# Revit family: Window-Double_Hung-Pella-Architect_Series-Vent
name_source: partatom
category: Windows
revit_build: Autodesk Revit Architecture 2013 (Build: 20130531_2115(x64)
units: mm (PartAtom-declared; Revit-internal decimal feet)

## types (80) — shared parameters
Analytic Construction = <None>
Architectural Design Manual = To be Determined
Construction Type = -
Cross Grille Pattern = No
Custom Grille Pattern = No
Custom Horizontal Lites = 2
Custom Vertical Lites = 3
Default Sill Height = 2' - 7 1/2"
Description = Double Hung - Vent Units
Egress Window = No
Energy Efficiency = http://www.pella.com
Environmental Commitment = http://www.pella.com
Ext Finish = Aluminum - Pella - Brown
Glazing Finish = Glass - Pella - Clear Insulating Glass
Glazing Thickness = 0' - 0 163/256"
Heat Transfer Coefficient (U) = 0.1000 BTU/(h·ft²·°F)
Int Finish = Wood - Pella - Pine
Lower Grille Visibility = Yes
Manufacturer = Pella Windows & Doors
Operation = Vent
Prairie Grille Pattern = No
Product Documentation Link = http://media.pella.com
Product Name = Architect Series Double-Hung Window
Product Page URL = http://www.pella.com
Series = Architect Series - Aluminum-Clad Wood
Size Constraint = Window Sizing constraints available in 6.35 mm increments
Thermal Resistance (R) = 10.0000 (h·ft²·°F)/BTU
Top Row Grille Pattern = No
Traditional Grille Pattern = Yes
URL = www.pella.com
Upper Grille Visibility = Yes
Wall Closure = By host
zero-valued in all types: Solar Heat Gain Coefficient, Visual Light Transmittance

## per-type parameters (varying)
| type | Bottom Pane Height | Checkrail Height | Head Height | Height | Rough Height | Rough Width | Unit Height | Unit Width | Width |
| 2135 | 1' - 5 15/64" | 1' - 5 7/8" | 5' - 6 1/2" | 2' - 11" | 2' - 11 3/4" | 1' - 9 3/4" | 2' - 11" | 1' - 9" | 1' - 9" |
| 2141 | 1' - 8 15/64" | 1' - 8 7/8" | 6' - 0 1/2" | 3' - 5" | 3' - 5 3/4" | 1' - 9 3/4" | 3' - 5" | 1' - 9" | 1' - 9" |
| 2147 | 1' - 11 15/64" | 1' - 11 7/8" | 6' - 6 1/2" | 3' - 11" | 3' - 11 3/4" | 1' - 9 3/4" | 3' - 11" | 1' - 9" | 1' - 9" |
| 2153 | 2' - 2 15/64" | 2' - 2 7/8" | 7' - 0 1/2" | 4' - 5" | 4' - 5 3/4" | 1' - 9 3/4" | 4' - 5" | 1' - 9" | 1' - 9" |
| 2157 | 2' - 4 15/64" | 2' - 4 7/8" | 7' - 4 1/2" | 4' - 9" | 4' - 9 3/4" | 1' - 9 3/4" | 4' - 9" | 1' - 9" | 1' - 9" |
| 2159 | 2' - 5 15/64" | 2' - 5 7/8" | 7' - 6 1/2" | 4' - 11" | 4' - 11 3/4" | 1' - 9 3/4" | 4' - 11" | 1' - 9" | 1' - 9" |
| 2165 | 2' - 8 15/64" | 2' - 8 7/8" | 8' - 0 1/2" | 5' - 5" | 5' - 5 3/4" | 1' - 9 3/4" | 5' - 5" | 1' - 9" | 1' - 9" |
| 2171 | 2' - 11 15/64" | 2' - 11 7/8" | 8' - 6 1/2" | 5' - 11" | 5' - 11 3/4" | 1' - 9 3/4" | 5' - 11" | 1' - 9" | 1' - 9" |
| 2177 | 3' - 2 15/64" | 3' - 2 7/8" | 9' - 0 1/2" | 6' - 5" | 6' - 5 3/4" | 1' - 9 3/4" | 6' - 5" | 1' - 9" | 1' - 9" |
| 2184 | 3' - 5 47/64" | 3' - 6 3/8" | 9' - 7 1/2" | 7' - 0" | 7' - 0 3/4" | 1' - 9 3/4" | 7' - 0" | 1' - 9" | 1' - 9" |
| 2535 | 1' - 5 15/64" | 1' - 5 7/8" | 5' - 6 1/2" | 2' - 11" | 2' - 11 3/4" | 2' - 1 3/4" | 2' - 11" | 2' - 1" | 2' - 1" |
| 2541 | 1' - 8 15/64" | 1' - 8 7/8" | 6' - 0 1/2" | 3' - 5" | 3' - 5 3/4" | 2' - 1 3/4" | 3' - 5" | 2' - 1" | 2' - 1" |
| 2547 | 1' - 11 15/64" | 1' - 11 7/8" | 6' - 6 1/2" | 3' - 11" | 3' - 11 3/4" | 2' - 1 3/4" | 3' - 11" | 2' - 1" | 2' - 1" |
| 2553 | 2' - 2 15/64" | 2' - 2 7/8" | 7' - 0 1/2" | 4' - 5" | 4' - 5 3/4" | 2' - 1 3/4" | 4' - 5" | 2' - 1" | 2' - 1" |
| 2557 | 2' - 4 15/64" | 2' - 4 7/8" | 7' - 4 1/2" | 4' - 9" | 4' - 9 3/4" | 2' - 1 3/4" | 4' - 9" | 2' - 1" | 2' - 1" |
| 2559 | 2' - 5 15/64" | 2' - 5 7/8" | 7' - 6 1/2" | 4' - 11" | 4' - 11 3/4" | 2' - 1 3/4" | 4' - 11" | 2' - 1" | 2' - 1" |
| 2565 | 2' - 8 15/64" | 2' - 8 7/8" | 8' - 0 1/2" | 5' - 5" | 5' - 5 3/4" | 2' - 1 3/4" | 5' - 5" | 2' - 1" | 2' - 1" |
| 2571 | 2' - 11 15/64" | 2' - 11 7/8" | 8' - 6 1/2" | 5' - 11" | 5' - 11 3/4" | 2' - 1 3/4" | 5' - 11" | 2' - 1" | 2' - 1" |
| 2577 | 3' - 2 15/64" | 3' - 2 7/8" | 9' - 0 1/2" | 6' - 5" | 6' - 5 3/4" | 2' - 1 3/4" | 6' - 5" | 2' - 1" | 2' - 1" |
| 2584 | 3' - 5 47/64" | 3' - 6 3/8" | 9' - 7 1/2" | 7' - 0" | 7' - 0 3/4" | 2' - 1 3/4" | 7' - 0" | 2' - 1" | 2' - 1" |
| 2935 | 1' - 5 15/64" | 1' - 5 7/8" | 5' - 6 1/2" | 2' - 11" | 2' - 11 3/4" | 2' - 5 3/4" | 2' - 11" | 2' - 5" | 2' - 5" |
| 2941 | 1' - 8 15/64" | 1' - 8 7/8" | 6' - 0 1/2" | 3' - 5" | 3' - 5 3/4" | 2' - 5 3/4" | 3' - 5" | 2' - 5" | 2' - 5" |
| 2947 | 1' - 11 15/64" | 1' - 11 7/8" | 6' - 6 1/2" | 3' - 11" | 3' - 11 3/4" | 2' - 5 3/4" | 3' - 11" | 2' - 5" | 2' - 5" |
| 2953 | 2' - 2 15/64" | 2' - 2 7/8" | 7' - 0 1/2" | 4' - 5" | 4' - 5 3/4" | 2' - 5 3/4" | 4' - 5" | 2' - 5" | 2' - 5" |
| 2957 | 2' - 4 15/64" | 2' - 4 7/8" | 7' - 4 1/2" | 4' - 9" | 4' - 9 3/4" | 2' - 5 3/4" | 4' - 9" | 2' - 5" | 2' - 5" |
| 2959 | 2' - 5 15/64" | 2' - 5 7/8" | 7' - 6 1/2" | 4' - 11" | 4' - 11 3/4" | 2' - 5 3/4" | 4' - 11" | 2' - 5" | 2' - 5" |
| 2965 | 2' - 8 15/64" | 2' - 8 7/8" | 8' - 0 1/2" | 5' - 5" | 5' - 5 3/4" | 2' - 5 3/4" | 5' - 5" | 2' - 5" | 2' - 5" |
| 2971 | 2' - 11 15/64" | 2' - 11 7/8" | 8' - 6 1/2" | 5' - 11" | 5' - 11 3/4" | 2' - 5 3/4" | 5' - 11" | 2' - 5" | 2' - 5" |
| 2977 | 3' - 2 15/64" | 3' - 2 7/8" | 9' - 0 1/2" | 6' - 5" | 6' - 5 3/4" | 2' - 5 3/4" | 6' - 5" | 2' - 5" | 2' - 5" |
| 2984 | 3' - 5 47/64" | 3' - 6 3/8" | 9' - 7 1/2" | 7' - 0" | 7' - 0 3/4" | 2' - 5 3/4" | 7' - 0" | 2' - 5" | 2' - 5" |
| 3335 | 1' - 5 15/64" | 1' - 5 7/8" | 5' - 6 1/2" | 2' - 11" | 2' - 11 3/4" | 2' - 9 3/4" | 2' - 11" | 2' - 9" | 2' - 9" |
| 3341 | 1' - 8 15/64" | 1' - 8 7/8" | 6' - 0 1/2" | 3' - 5" | 3' - 5 3/4" | 2' - 9 3/4" | 3' - 5" | 2' - 9" | 2' - 9" |
| 3347 | 1' - 11 15/64" | 1' - 11 7/8" | 6' - 6 1/2" | 3' - 11" | 3' - 11 3/4" | 2' - 9 3/4" | 3' - 11" | 2' - 9" | 2' - 9" |
| 3353 | 2' - 2 15/64" | 2' - 2 7/8" | 7' - 0 1/2" | 4' - 5" | 4' - 5 3/4" | 2' - 9 3/4" | 4' - 5" | 2' - 9" | 2' - 9" |
| 3357 | 2' - 4 15/64" | 2' - 4 7/8" | 7' - 4 1/2" | 4' - 9" | 4' - 9 3/4" | 2' - 9 3/4" | 4' - 9" | 2' - 9" | 2' - 9" |
| 3359 | 2' - 5 15/64" | 2' - 5 7/8" | 7' - 6 1/2" | 4' - 11" | 4' - 11 3/4" | 2' - 9 3/4" | 4' - 11" | 2' - 9" | 2' - 9" |
| 3365 | 2' - 8 15/64" | 2' - 8 7/8" | 8' - 0 1/2" | 5' - 5" | 5' - 5 3/4" | 2' - 9 3/4" | 5' - 5" | 2' - 9" | 2' - 9" |
| 3371 | 2' - 11 15/64" | 2' - 11 7/8" | 8' - 6 1/2" | 5' - 11" | 5' - 11 3/4" | 2' - 9 3/4" | 5' - 11" | 2' - 9" | 2' - 9" |
| 3377 | 3' - 2 15/64" | 3' - 2 7/8" | 9' - 0 1/2" | 6' - 5" | 6' - 5 3/4" | 2' - 9 3/4" | 6' - 5" | 2' - 9" | 2' - 9" |
| 3384 | 3' - 5 47/64" | 3' - 6 3/8" | 9' - 7 1/2" | 7' - 0" | 7' - 0 3/4" | 2' - 9 3/4" | 7' - 0" | 2' - 9" | 2' - 9" |
| 3735 | 1' - 5 15/64" | 1' - 5 7/8" | 5' - 6 1/2" | 2' - 11" | 2' - 11 3/4" | 3' - 1 3/4" | 2' - 11" | 3' - 1" | 3' - 1" |
| 3741 | 1' - 8 15/64" | 1' - 8 7/8" | 6' - 0 1/2" | 3' - 5" | 3' - 5 3/4" | 3' - 1 3/4" | 3' - 5" | 3' - 1" | 3' - 1" |
| 3747 | 1' - 11 15/64" | 1' - 11 7/8" | 6' - 6 1/2" | 3' - 11" | 3' - 11 3/4" | 3' - 1 3/4" | 3' - 11" | 3' - 1" | 3' - 1" |
| 3753 | 2' - 2 15/64" | 2' - 2 7/8" | 7' - 0 1/2" | 4' - 5" | 4' - 5 3/4" | 3' - 1 3/4" | 4' - 5" | 3' - 1" | 3' - 1" |
| 3757 | 2' - 4 15/64" | 2' - 4 7/8" | 7' - 4 1/2" | 4' - 9" | 4' - 9 3/4" | 3' - 1 3/4" | 4' - 9" | 3' - 1" | 3' - 1" |
| 3759 | 2' - 5 15/64" | 2' - 5 7/8" | 7' - 6 1/2" | 4' - 11" | 4' - 11 3/4" | 3' - 1 3/4" | 4' - 11" | 3' - 1" | 3' - 1" |
| 3765 | 2' - 8 15/64" | 2' - 8 7/8" | 8' - 0 1/2" | 5' - 5" | 5' - 5 3/4" | 3' - 1 3/4" | 5' - 5" | 3' - 1" | 3' - 1" |
| 3771 | 2' - 11 15/64" | 2' - 11 7/8" | 8' - 6 1/2" | 5' - 11" | 5' - 11 3/4" | 3' - 1 3/4" | 5' - 11" | 3' - 1" | 3' - 1" |
| 3777 | 3' - 2 15/64" | 3' - 2 7/8" | 9' - 0 1/2" | 6' - 5" | 6' - 5 3/4" | 3' - 1 3/4" | 6' - 5" | 3' - 1" | 3' - 1" |
| 3784 | 3' - 5 47/64" | 3' - 6 3/8" | 9' - 7 1/2" | 7' - 0" | 7' - 0 3/4" | 3' - 1 3/4" | 7' - 0" | 3' - 1" | 3' - 1" |
| 4135 | 1' - 5 15/64" | 1' - 5 7/8" | 5' - 6 1/2" | 2' - 11" | 2' - 11 3/4" | 3' - 5 3/4" | 2' - 11" | 3' - 5" | 3' - 5" |
| 4141 | 1' - 8 15/64" | 1' - 8 7/8" | 6' - 0 1/2" | 3' - 5" | 3' - 5 3/4" | 3' - 5 3/4" | 3' - 5" | 3' - 5" | 3' - 5" |
| 4147 | 1' - 11 15/64" | 1' - 11 7/8" | 6' - 6 1/2" | 3' - 11" | 3' - 11 3/4" | 3' - 5 3/4" | 3' - 11" | 3' - 5" | 3' - 5" |
| 4153 | 2' - 2 15/64" | 2' - 2 7/8" | 7' - 0 1/2" | 4' - 5" | 4' - 5 3/4" | 3' - 5 3/4" | 4' - 5" | 3' - 5" | 3' - 5" |
| 4157 | 2' - 4 15/64" | 2' - 4 7/8" | 7' - 4 1/2" | 4' - 9" | 4' - 9 3/4" | 3' - 5 3/4" | 4' - 9" | 3' - 5" | 3' - 5" |
| 4159 | 2' - 5 15/64" | 2' - 5 7/8" | 7' - 6 1/2" | 4' - 11" | 4' - 11 3/4" | 3' - 5 3/4" | 4' - 11" | 3' - 5" | 3' - 5" |
| 4165 | 2' - 8 15/64" | 2' - 8 7/8" | 8' - 0 1/2" | 5' - 5" | 5' - 5 3/4" | 3' - 5 3/4" | 5' - 5" | 3' - 5" | 3' - 5" |
| 4171 | 2' - 11 15/64" | 2' - 11 7/8" | 8' - 6 1/2" | 5' - 11" | 5' - 11 3/4" | 3' - 5 3/4" | 5' - 11" | 3' - 5" | 3' - 5" |
| 4177 | 3' - 2 15/64" | 3' - 2 7/8" | 9' - 0 1/2" | 6' - 5" | 6' - 5 3/4" | 3' - 5 3/4" | 6' - 5" | 3' - 5" | 3' - 5" |
| 4184 | 3' - 5 47/64" | 3' - 6 3/8" | 9' - 7 1/2" | 7' - 0" | 7' - 0 3/4" | 3' - 5 3/4" | 7' - 0" | 3' - 5" | 3' - 5" |
| 4535 | 1' - 5 15/64" | 1' - 5 7/8" | 5' - 6 1/2" | 2' - 11" | 2' - 11 3/4" | 3' - 9 3/4" | 2' - 11" | 3' - 9" | 3' - 9" |
| 4541 | 1' - 8 15/64" | 1' - 8 7/8" | 6' - 0 1/2" | 3' - 5" | 3' - 5 3/4" | 3' - 9 3/4" | 3' - 5" | 3' - 9" | 3' - 9" |
| 4547 | 1' - 11 15/64" | 1' - 11 7/8" | 6' - 6 1/2" | 3' - 11" | 3' - 11 3/4" | 3' - 9 3/4" | 3' - 11" | 3' - 9" | 3' - 9" |
| 4553 | 2' - 2 15/64" | 2' - 2 7/8" | 7' - 0 1/2" | 4' - 5" | 4' - 5 3/4" | 3' - 9 3/4" | 4' - 5" | 3' - 9" | 3' - 9" |
| 4557 | 2' - 4 15/64" | 2' - 4 7/8" | 7' - 4 1/2" | 4' - 9" | 4' - 9 3/4" | 3' - 9 3/4" | 4' - 9" | 3' - 9" | 3' - 9" |
| 4559 | 2' - 5 15/64" | 2' - 5 7/8" | 7' - 6 1/2" | 4' - 11" | 4' - 11 3/4" | 3' - 9 3/4" | 4' - 11" | 3' - 9" | 3' - 9" |
| 4565 | 2' - 8 15/64" | 2' - 8 7/8" | 8' - 0 1/2" | 5' - 5" | 5' - 5 3/4" | 3' - 9 3/4" | 5' - 5" | 3' - 9" | 3' - 9" |
| 4571 | 2' - 11 15/64" | 2' - 11 7/8" | 8' - 6 1/2" | 5' - 11" | 5' - 11 3/4" | 3' - 9 3/4" | 5' - 11" | 3' - 9" | 3' - 9" |
| 4577 | 3' - 2 15/64" | 3' - 2 7/8" | 9' - 0 1/2" | 6' - 5" | 6' - 5 3/4" | 3' - 9 3/4" | 6' - 5" | 3' - 9" | 3' - 9" |
| 4584 | 3' - 5 47/64" | 3' - 6 3/8" | 9' - 7 1/2" | 7' - 0" | 7' - 0 3/4" | 3' - 9 3/4" | 7' - 0" | 3' - 9" | 3' - 9" |
| 4835 | 1' - 5 15/64" | 1' - 5 7/8" | 5' - 6 1/2" | 2' - 11" | 2' - 11 3/4" | 4' - 0 3/4" | 2' - 11" | 4' - 0" | 4' - 0" |
| 4841 | 1' - 8 15/64" | 1' - 8 7/8" | 6' - 0 1/2" | 3' - 5" | 3' - 5 3/4" | 4' - 0 3/4" | 3' - 5" | 4' - 0" | 4' - 0" |
| 4847 | 1' - 11 15/64" | 1' - 11 7/8" | 6' - 6 1/2" | 3' - 11" | 3' - 11 3/4" | 4' - 0 3/4" | 3' - 11" | 4' - 0" | 4' - 0" |
| 4853 | 2' - 2 15/64" | 2' - 2 7/8" | 7' - 0 1/2" | 4' - 5" | 4' - 5 3/4" | 4' - 0 3/4" | 4' - 5" | 4' - 0" | 4' - 0" |
| 4857 | 2' - 4 15/64" | 2' - 4 7/8" | 7' - 4 1/2" | 4' - 9" | 4' - 9 3/4" | 4' - 0 3/4" | 4' - 9" | 4' - 0" | 4' - 0" |
| 4859 | 2' - 5 15/64" | 2' - 5 7/8" | 7' - 6 1/2" | 4' - 11" | 4' - 11 3/4" | 4' - 0 3/4" | 4' - 11" | 4' - 0" | 4' - 0" |
| 4865 | 2' - 8 15/64" | 2' - 8 7/8" | 8' - 0 1/2" | 5' - 5" | 5' - 5 3/4" | 4' - 0 3/4" | 5' - 5" | 4' - 0" | 4' - 0" |
| 4871 | 2' - 11 15/64" | 2' - 11 7/8" | 8' - 6 1/2" | 5' - 11" | 5' - 11 3/4" | 4' - 0 3/4" | 5' - 11" | 4' - 0" | 4' - 0" |
| 4877 | 3' - 2 15/64" | 3' - 2 7/8" | 9' - 0 1/2" | 6' - 5" | 6' - 5 3/4" | 4' - 0 3/4" | 6' - 5" | 4' - 0" | 4' - 0" |
| 4884 | 3' - 5 47/64" | 3' - 6 3/8" | 9' - 7 1/2" | 7' - 0" | 7' - 0 3/4" | 4' - 0 3/4" | 7' - 0" | 4' - 0" | 4' - 0" |

note: column(s) folded — value = type name in every type: Model

## geometry (parser evidence)
native form markers: Blend x10, Sweep x11
no freeform markers — native parametric forms only
